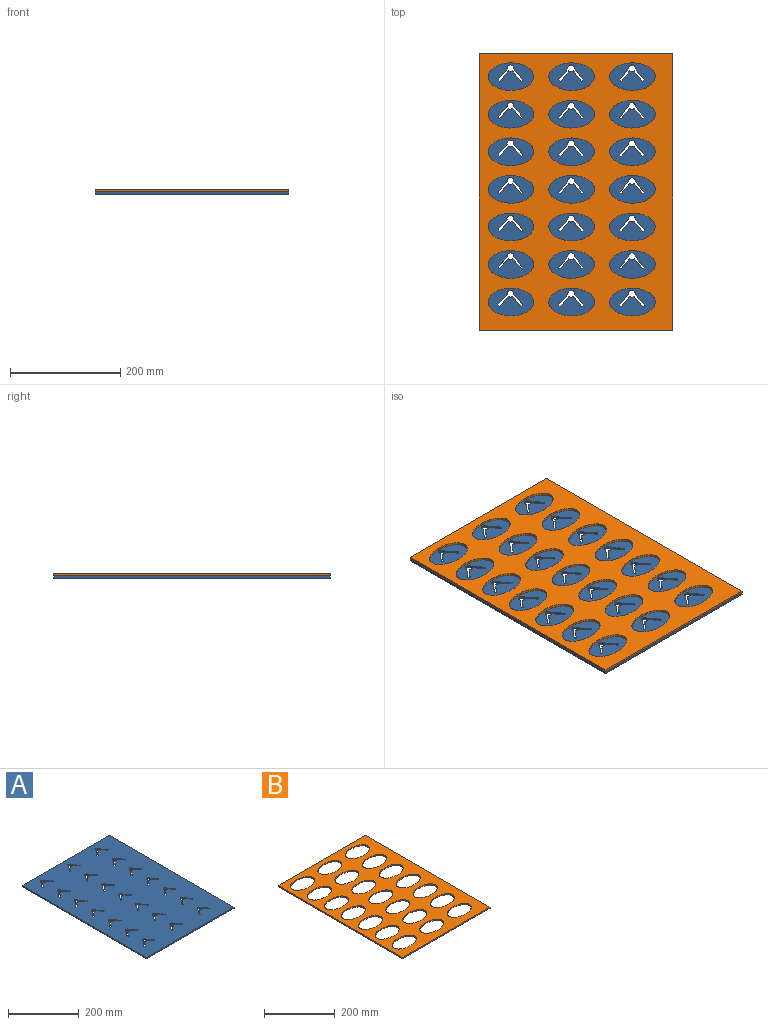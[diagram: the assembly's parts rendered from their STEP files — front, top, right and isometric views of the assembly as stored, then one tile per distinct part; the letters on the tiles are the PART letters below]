
ASSEMBLY  parts=2 mates=1
PART A: 174 faces, bbox 350x500x4 mm
  f0: plane 500x350mm, normal (0,0,1), area 168404.2mm2, adj f2,f3,f4,f5,f6,f7,f8,f9
  f1: plane 500x350mm, normal (0,0,-1), area 168404.2mm2, adj f2,f3,f4,f5,f6,f7,f8,f9
  f2: plane 350x4mm, normal (0,-1,0), area 1400mm2, adj f0,f1,f3,f5
  f3: plane 500x4mm, normal (1,0,0), area 2000mm2, adj f0,f1,f2,f4
  f4: plane 350x4mm, normal (0,1,0), area 1400mm2, adj f0,f1,f3,f5
  f5: plane 500x4mm, normal (-1,0,0), area 2000mm2, adj f0,f1,f2,f4
  f6: plane 19.38x16.26mm, normal (-0.77,-0.64,0), area 101.2mm2, adj f0,f1,f7,f13
  f7: cylinder r=6.17mm len=12.35mm, axis (0,0,1), area 85.9mm2, adj f0,f1,f6,f8
  f8: plane 19.38x16.26mm, normal (0.77,-0.64,0), area 101.2mm2, adj f0,f1,f7,f9
  f9: plane 4x3.06mm, normal (0.64,0.77,0), area 16mm2, adj f0,f1,f8,f10
  f10: plane 18.25x15.31mm, normal (-0.77,0.64,0), area 95.3mm2, adj f0,f1,f9,f11
  f11: cylinder r=6.17mm len=7.94mm, axis (0,0,1), area 34.5mm2, adj f0,f1,f10,f12
  f12: plane 18.25x15.31mm, normal (0.77,0.64,0), area 95.3mm2, adj f0,f1,f11,f13
  f13: plane 4x3.06mm, normal (-0.64,0.77,0), area 16mm2, adj f0,f1,f6,f12
  f14: cylinder r=6.17mm len=7.94mm, axis (0,0,1), area 34.5mm2, adj f0,f1,f15,f21
  f15: plane 18.25x15.31mm, normal (0.77,0.64,0), area 95.3mm2, adj f0,f1,f14,f16
  f16: plane 4x3.06mm, normal (-0.64,0.77,0), area 16mm2, adj f0,f1,f15,f17
  f17: plane 19.38x16.26mm, normal (-0.77,-0.64,0), area 101.2mm2, adj f0,f1,f16,f18
  f18: cylinder r=6.17mm len=12.35mm, axis (0,0,1), area 85.9mm2, adj f0,f1,f17,f19
  f19: plane 19.38x16.26mm, normal (0.77,-0.64,0), area 101.2mm2, adj f0,f1,f18,f20
  f20: plane 4x3.06mm, normal (0.64,0.77,0), area 16mm2, adj f0,f1,f19,f21
  f21: plane 18.25x15.31mm, normal (-0.77,0.64,0), area 95.3mm2, adj f0,f1,f14,f20
  f22: cylinder r=6.17mm len=7.94mm, axis (0,0,1), area 34.5mm2, adj f0,f1,f23,f29
  f23: plane 18.25x15.31mm, normal (0.77,0.64,0), area 95.3mm2, adj f0,f1,f22,f24
  f24: plane 4x3.06mm, normal (-0.64,0.77,0), area 16mm2, adj f0,f1,f23,f25
  f25: plane 19.38x16.26mm, normal (-0.77,-0.64,0), area 101.2mm2, adj f0,f1,f24,f26
  f26: cylinder r=6.17mm len=12.35mm, axis (0,0,1), area 85.9mm2, adj f0,f1,f25,f27
  f27: plane 19.38x16.26mm, normal (0.77,-0.64,0), area 101.2mm2, adj f0,f1,f26,f28
  f28: plane 4x3.06mm, normal (0.64,0.77,0), area 16mm2, adj f0,f1,f27,f29
  f29: plane 18.25x15.31mm, normal (-0.77,0.64,0), area 95.3mm2, adj f0,f1,f22,f28
  f30: cylinder r=6.17mm len=7.94mm, axis (0,0,1), area 34.5mm2, adj f0,f1,f31,f37
  f31: plane 18.25x15.31mm, normal (0.77,0.64,0), area 95.3mm2, adj f0,f1,f30,f32
  f32: plane 4x3.06mm, normal (-0.64,0.77,0), area 16mm2, adj f0,f1,f31,f33
  f33: plane 19.38x16.26mm, normal (-0.77,-0.64,0), area 101.2mm2, adj f0,f1,f32,f34
  f34: cylinder r=6.17mm len=12.35mm, axis (0,0,1), area 85.9mm2, adj f0,f1,f33,f35
  f35: plane 19.38x16.26mm, normal (0.77,-0.64,0), area 101.2mm2, adj f0,f1,f34,f36
  f36: plane 4x3.06mm, normal (0.64,0.77,0), area 16mm2, adj f0,f1,f35,f37
  f37: plane 18.25x15.31mm, normal (-0.77,0.64,0), area 95.3mm2, adj f0,f1,f30,f36
  f38: cylinder r=6.17mm len=7.94mm, axis (0,0,1), area 34.5mm2, adj f0,f1,f39,f45
  f39: plane 18.25x15.31mm, normal (0.77,0.64,0), area 95.3mm2, adj f0,f1,f38,f40
  f40: plane 4x3.06mm, normal (-0.64,0.77,0), area 16mm2, adj f0,f1,f39,f41
  f41: plane 19.38x16.26mm, normal (-0.77,-0.64,0), area 101.2mm2, adj f0,f1,f40,f42
  f42: cylinder r=6.17mm len=12.35mm, axis (0,0,1), area 85.9mm2, adj f0,f1,f41,f43
  f43: plane 19.38x16.26mm, normal (0.77,-0.64,0), area 101.2mm2, adj f0,f1,f42,f44
  f44: plane 4x3.06mm, normal (0.64,0.77,0), area 16mm2, adj f0,f1,f43,f45
  f45: plane 18.25x15.31mm, normal (-0.77,0.64,0), area 95.3mm2, adj f0,f1,f38,f44
  f46: cylinder r=6.17mm len=7.94mm, axis (0,0,1), area 34.5mm2, adj f0,f1,f47,f53
  f47: plane 18.25x15.31mm, normal (0.77,0.64,0), area 95.3mm2, adj f0,f1,f46,f48
  f48: plane 4x3.06mm, normal (-0.64,0.77,0), area 16mm2, adj f0,f1,f47,f49
  f49: plane 19.38x16.26mm, normal (-0.77,-0.64,0), area 101.2mm2, adj f0,f1,f48,f50
  f50: cylinder r=6.17mm len=12.35mm, axis (0,0,1), area 85.9mm2, adj f0,f1,f49,f51
  f51: plane 19.38x16.26mm, normal (0.77,-0.64,0), area 101.2mm2, adj f0,f1,f50,f52
  f52: plane 4x3.06mm, normal (0.64,0.77,0), area 16mm2, adj f0,f1,f51,f53
  f53: plane 18.25x15.31mm, normal (-0.77,0.64,0), area 95.3mm2, adj f0,f1,f46,f52
  f54: cylinder r=6.17mm len=7.94mm, axis (0,0,1), area 34.5mm2, adj f0,f1,f55,f61
  f55: plane 18.25x15.31mm, normal (0.77,0.64,0), area 95.3mm2, adj f0,f1,f54,f56
  f56: plane 4x3.06mm, normal (-0.64,0.77,0), area 16mm2, adj f0,f1,f55,f57
  f57: plane 19.38x16.26mm, normal (-0.77,-0.64,0), area 101.2mm2, adj f0,f1,f56,f58
  f58: cylinder r=6.17mm len=12.35mm, axis (0,0,1), area 85.9mm2, adj f0,f1,f57,f59
  f59: plane 19.38x16.26mm, normal (0.77,-0.64,0), area 101.2mm2, adj f0,f1,f58,f60
  f60: plane 4x3.06mm, normal (0.64,0.77,0), area 16mm2, adj f0,f1,f59,f61
  f61: plane 18.25x15.31mm, normal (-0.77,0.64,0), area 95.3mm2, adj f0,f1,f54,f60
  f62: cylinder r=6.17mm len=7.94mm, axis (0,0,1), area 34.5mm2, adj f0,f1,f63,f69
  f63: plane 18.25x15.31mm, normal (0.77,0.64,0), area 95.3mm2, adj f0,f1,f62,f64
  f64: plane 4x3.06mm, normal (-0.64,0.77,0), area 16mm2, adj f0,f1,f63,f65
  f65: plane 19.38x16.26mm, normal (-0.77,-0.64,0), area 101.2mm2, adj f0,f1,f64,f66
  f66: cylinder r=6.17mm len=12.35mm, axis (0,0,1), area 85.9mm2, adj f0,f1,f65,f67
  f67: plane 19.38x16.26mm, normal (0.77,-0.64,0), area 101.2mm2, adj f0,f1,f66,f68
  f68: plane 4x3.06mm, normal (0.64,0.77,0), area 16mm2, adj f0,f1,f67,f69
  f69: plane 18.25x15.31mm, normal (-0.77,0.64,0), area 95.3mm2, adj f0,f1,f62,f68
  f70: cylinder r=6.17mm len=7.94mm, axis (0,0,1), area 34.5mm2, adj f0,f1,f71,f77
  f71: plane 18.25x15.31mm, normal (0.77,0.64,0), area 95.3mm2, adj f0,f1,f70,f72
  f72: plane 4x3.06mm, normal (-0.64,0.77,0), area 16mm2, adj f0,f1,f71,f73
  f73: plane 19.38x16.26mm, normal (-0.77,-0.64,0), area 101.2mm2, adj f0,f1,f72,f74
  f74: cylinder r=6.17mm len=12.35mm, axis (0,0,1), area 85.9mm2, adj f0,f1,f73,f75
  f75: plane 19.38x16.26mm, normal (0.77,-0.64,0), area 101.2mm2, adj f0,f1,f74,f76
  f76: plane 4x3.06mm, normal (0.64,0.77,0), area 16mm2, adj f0,f1,f75,f77
  f77: plane 18.25x15.31mm, normal (-0.77,0.64,0), area 95.3mm2, adj f0,f1,f70,f76
  f78: cylinder r=6.17mm len=7.94mm, axis (0,0,1), area 34.5mm2, adj f0,f1,f79,f85
  f79: plane 18.25x15.31mm, normal (0.77,0.64,0), area 95.3mm2, adj f0,f1,f78,f80
  f80: plane 4x3.06mm, normal (-0.64,0.77,0), area 16mm2, adj f0,f1,f79,f81
  f81: plane 19.38x16.26mm, normal (-0.77,-0.64,0), area 101.2mm2, adj f0,f1,f80,f82
  f82: cylinder r=6.17mm len=12.35mm, axis (0,0,1), area 85.9mm2, adj f0,f1,f81,f83
  f83: plane 19.38x16.26mm, normal (0.77,-0.64,0), area 101.2mm2, adj f0,f1,f82,f84
  f84: plane 4x3.06mm, normal (0.64,0.77,0), area 16mm2, adj f0,f1,f83,f85
  f85: plane 18.25x15.31mm, normal (-0.77,0.64,0), area 95.3mm2, adj f0,f1,f78,f84
  f86: cylinder r=6.17mm len=7.94mm, axis (0,0,1), area 34.5mm2, adj f0,f1,f87,f93
  f87: plane 18.25x15.31mm, normal (0.77,0.64,0), area 95.3mm2, adj f0,f1,f86,f88
  f88: plane 4x3.06mm, normal (-0.64,0.77,0), area 16mm2, adj f0,f1,f87,f89
  f89: plane 19.38x16.26mm, normal (-0.77,-0.64,0), area 101.2mm2, adj f0,f1,f88,f90
  f90: cylinder r=6.17mm len=12.35mm, axis (0,0,1), area 85.9mm2, adj f0,f1,f89,f91
  f91: plane 19.38x16.26mm, normal (0.77,-0.64,0), area 101.2mm2, adj f0,f1,f90,f92
  f92: plane 4x3.06mm, normal (0.64,0.77,0), area 16mm2, adj f0,f1,f91,f93
  f93: plane 18.25x15.31mm, normal (-0.77,0.64,0), area 95.3mm2, adj f0,f1,f86,f92
  f94: cylinder r=6.17mm len=7.94mm, axis (0,0,1), area 34.5mm2, adj f0,f1,f95,f101
  f95: plane 18.25x15.31mm, normal (0.77,0.64,0), area 95.3mm2, adj f0,f1,f94,f96
  f96: plane 4x3.06mm, normal (-0.64,0.77,0), area 16mm2, adj f0,f1,f95,f97
  f97: plane 19.38x16.26mm, normal (-0.77,-0.64,0), area 101.2mm2, adj f0,f1,f96,f98
  f98: cylinder r=6.17mm len=12.35mm, axis (0,0,1), area 85.9mm2, adj f0,f1,f97,f99
  f99: plane 19.38x16.26mm, normal (0.77,-0.64,0), area 101.2mm2, adj f0,f1,f98,f100
  f100: plane 4x3.06mm, normal (0.64,0.77,0), area 16mm2, adj f0,f1,f99,f101
  f101: plane 18.25x15.31mm, normal (-0.77,0.64,0), area 95.3mm2, adj f0,f1,f94,f100
  f102: plane 4x3.06mm, normal (0.64,0.77,0), area 16mm2, adj f0,f1,f103,f109
  f103: plane 18.25x15.31mm, normal (-0.77,0.64,0), area 95.3mm2, adj f0,f1,f102,f104
  f104: cylinder r=6.17mm len=7.94mm, axis (0,0,1), area 34.5mm2, adj f0,f1,f103,f105
  f105: plane 18.25x15.31mm, normal (0.77,0.64,0), area 95.3mm2, adj f0,f1,f104,f106
  f106: plane 4x3.06mm, normal (-0.64,0.77,0), area 16mm2, adj f0,f1,f105,f107
  f107: plane 19.38x16.26mm, normal (-0.77,-0.64,0), area 101.2mm2, adj f0,f1,f106,f108
  f108: cylinder r=6.17mm len=12.35mm, axis (0,0,1), area 85.9mm2, adj f0,f1,f107,f109
  f109: plane 19.38x16.26mm, normal (0.77,-0.64,0), area 101.2mm2, adj f0,f1,f102,f108
  f110: cylinder r=6.17mm len=7.94mm, axis (0,0,1), area 34.5mm2, adj f0,f1,f111,f117
  f111: plane 18.25x15.31mm, normal (0.77,0.64,0), area 95.3mm2, adj f0,f1,f110,f112
  f112: plane 4x3.06mm, normal (-0.64,0.77,0), area 16mm2, adj f0,f1,f111,f113
  f113: plane 19.38x16.26mm, normal (-0.77,-0.64,0), area 101.2mm2, adj f0,f1,f112,f114
  f114: cylinder r=6.17mm len=12.35mm, axis (0,0,1), area 85.9mm2, adj f0,f1,f113,f115
  f115: plane 19.38x16.26mm, normal (0.77,-0.64,0), area 101.2mm2, adj f0,f1,f114,f116
  f116: plane 4x3.06mm, normal (0.64,0.77,0), area 16mm2, adj f0,f1,f115,f117
  f117: plane 18.25x15.31mm, normal (-0.77,0.64,0), area 95.3mm2, adj f0,f1,f110,f116
  f118: cylinder r=6.17mm len=7.94mm, axis (0,0,1), area 34.5mm2, adj f0,f1,f119,f125
  f119: plane 18.25x15.31mm, normal (0.77,0.64,0), area 95.3mm2, adj f0,f1,f118,f120
  f120: plane 4x3.06mm, normal (-0.64,0.77,0), area 16mm2, adj f0,f1,f119,f121
  f121: plane 19.38x16.26mm, normal (-0.77,-0.64,0), area 101.2mm2, adj f0,f1,f120,f122
  f122: cylinder r=6.17mm len=12.35mm, axis (0,0,1), area 85.9mm2, adj f0,f1,f121,f123
  f123: plane 19.38x16.26mm, normal (0.77,-0.64,0), area 101.2mm2, adj f0,f1,f122,f124
  f124: plane 4x3.06mm, normal (0.64,0.77,0), area 16mm2, adj f0,f1,f123,f125
  f125: plane 18.25x15.31mm, normal (-0.77,0.64,0), area 95.3mm2, adj f0,f1,f118,f124
  f126: cylinder r=6.17mm len=7.94mm, axis (0,0,1), area 34.5mm2, adj f0,f1,f127,f133
  f127: plane 18.25x15.31mm, normal (0.77,0.64,0), area 95.3mm2, adj f0,f1,f126,f128
  f128: plane 4x3.06mm, normal (-0.64,0.77,0), area 16mm2, adj f0,f1,f127,f129
  f129: plane 19.38x16.26mm, normal (-0.77,-0.64,0), area 101.2mm2, adj f0,f1,f128,f130
  f130: cylinder r=6.17mm len=12.35mm, axis (0,0,1), area 85.9mm2, adj f0,f1,f129,f131
  f131: plane 19.38x16.26mm, normal (0.77,-0.64,0), area 101.2mm2, adj f0,f1,f130,f132
  f132: plane 4x3.06mm, normal (0.64,0.77,0), area 16mm2, adj f0,f1,f131,f133
  f133: plane 18.25x15.31mm, normal (-0.77,0.64,0), area 95.3mm2, adj f0,f1,f126,f132
  f134: cylinder r=6.17mm len=7.94mm, axis (0,0,1), area 34.5mm2, adj f0,f1,f135,f141
  f135: plane 18.25x15.31mm, normal (0.77,0.64,0), area 95.3mm2, adj f0,f1,f134,f136
  f136: plane 4x3.06mm, normal (-0.64,0.77,0), area 16mm2, adj f0,f1,f135,f137
  f137: plane 19.38x16.26mm, normal (-0.77,-0.64,0), area 101.2mm2, adj f0,f1,f136,f138
  f138: cylinder r=6.17mm len=12.35mm, axis (0,0,1), area 85.9mm2, adj f0,f1,f137,f139
  f139: plane 19.38x16.26mm, normal (0.77,-0.64,0), area 101.2mm2, adj f0,f1,f138,f140
  f140: plane 4x3.06mm, normal (0.64,0.77,0), area 16mm2, adj f0,f1,f139,f141
  f141: plane 18.25x15.31mm, normal (-0.77,0.64,0), area 95.3mm2, adj f0,f1,f134,f140
  f142: cylinder r=6.17mm len=7.94mm, axis (0,0,1), area 34.5mm2, adj f0,f1,f143,f149
  f143: plane 18.25x15.31mm, normal (0.77,0.64,0), area 95.3mm2, adj f0,f1,f142,f144
  f144: plane 4x3.06mm, normal (-0.64,0.77,0), area 16mm2, adj f0,f1,f143,f145
  f145: plane 19.38x16.26mm, normal (-0.77,-0.64,0), area 101.2mm2, adj f0,f1,f144,f146
  f146: cylinder r=6.17mm len=12.35mm, axis (0,0,1), area 85.9mm2, adj f0,f1,f145,f147
  f147: plane 19.38x16.26mm, normal (0.77,-0.64,0), area 101.2mm2, adj f0,f1,f146,f148
  f148: plane 4x3.06mm, normal (0.64,0.77,0), area 16mm2, adj f0,f1,f147,f149
  f149: plane 18.25x15.31mm, normal (-0.77,0.64,0), area 95.3mm2, adj f0,f1,f142,f148
  f150: cylinder r=6.17mm len=7.94mm, axis (0,0,1), area 34.5mm2, adj f0,f1,f151,f157
  f151: plane 18.25x15.31mm, normal (0.77,0.64,0), area 95.3mm2, adj f0,f1,f150,f152
  f152: plane 4x3.06mm, normal (-0.64,0.77,0), area 16mm2, adj f0,f1,f151,f153
  f153: plane 19.38x16.26mm, normal (-0.77,-0.64,0), area 101.2mm2, adj f0,f1,f152,f154
  f154: cylinder r=6.17mm len=12.35mm, axis (0,0,1), area 85.9mm2, adj f0,f1,f153,f155
  f155: plane 19.38x16.26mm, normal (0.77,-0.64,0), area 101.2mm2, adj f0,f1,f154,f156
  f156: plane 4x3.06mm, normal (0.64,0.77,0), area 16mm2, adj f0,f1,f155,f157
  f157: plane 18.25x15.31mm, normal (-0.77,0.64,0), area 95.3mm2, adj f0,f1,f150,f156
  f158: cylinder r=6.17mm len=7.94mm, axis (0,0,1), area 34.5mm2, adj f0,f1,f159,f165
  f159: plane 18.25x15.31mm, normal (0.77,0.64,0), area 95.3mm2, adj f0,f1,f158,f160
  f160: plane 4x3.06mm, normal (-0.64,0.77,0), area 16mm2, adj f0,f1,f159,f161
  f161: plane 19.38x16.26mm, normal (-0.77,-0.64,0), area 101.2mm2, adj f0,f1,f160,f162
  f162: cylinder r=6.17mm len=12.35mm, axis (0,0,1), area 85.9mm2, adj f0,f1,f161,f163
  f163: plane 19.38x16.26mm, normal (0.77,-0.64,0), area 101.2mm2, adj f0,f1,f162,f164
  f164: plane 4x3.06mm, normal (0.64,0.77,0), area 16mm2, adj f0,f1,f163,f165
  f165: plane 18.25x15.31mm, normal (-0.77,0.64,0), area 95.3mm2, adj f0,f1,f158,f164
  f166: cylinder r=6.17mm len=7.94mm, axis (0,0,1), area 34.5mm2, adj f0,f1,f167,f173
  f167: plane 18.25x15.31mm, normal (0.77,0.64,0), area 95.3mm2, adj f0,f1,f166,f168
  f168: plane 4x3.06mm, normal (-0.64,0.77,0), area 16mm2, adj f0,f1,f167,f169
  f169: plane 19.38x16.26mm, normal (-0.77,-0.64,0), area 101.2mm2, adj f0,f1,f168,f170
  f170: cylinder r=6.17mm len=12.35mm, axis (0,0,1), area 85.9mm2, adj f0,f1,f169,f171
  f171: plane 19.38x16.26mm, normal (0.77,-0.64,0), area 101.2mm2, adj f0,f1,f170,f172
  f172: plane 4x3.06mm, normal (0.64,0.77,0), area 16mm2, adj f0,f1,f171,f173
  f173: plane 18.25x15.31mm, normal (-0.77,0.64,0), area 95.3mm2, adj f0,f1,f166,f172
PART B: 27 faces, bbox 350x500x4 mm
  f0: plane 350x4mm, normal (0,-1,0), area 1400mm2, adj f1,f3,f4,f5
  f1: plane 500x4mm, normal (1,0,0), area 2000mm2, adj f0,f2,f4,f5
  f2: plane 350x4mm, normal (0,1,0), area 1400mm2, adj f1,f3,f4,f5
  f3: plane 500x4mm, normal (-1,0,0), area 2000mm2, adj f0,f2,f4,f5
  f4: plane 500x350mm, normal (0,0,1), area 107068.3mm2, adj f0,f1,f2,f3,f6,f7,f8,f9
  f5: plane 500x350mm, normal (0,0,-1), area 107068.3mm2, adj f0,f1,f2,f3,f6,f7,f8,f9
  f6: extruded ~82.37x50mm, area 844.2mm2, adj f4,f5
  f7: extruded ~82.37x50mm, area 844.2mm2, adj f4,f5
  f8: extruded ~82.37x50mm, area 844.2mm2, adj f4,f5
  f9: extruded ~82.37x50mm, area 844.2mm2, adj f4,f5
  f10: extruded ~82.37x50mm, area 844.2mm2, adj f4,f5
  f11: extruded ~82.37x50mm, area 844.2mm2, adj f4,f5
  f12: extruded ~82.37x50mm, area 844.2mm2, adj f4,f5
  f13: extruded ~82.37x50mm, area 844.2mm2, adj f4,f5
  f14: extruded ~82.37x50mm, area 844.2mm2, adj f4,f5
  f15: extruded ~82.37x50mm, area 844.2mm2, adj f4,f5
  f16: extruded ~82.37x50mm, area 844.2mm2, adj f4,f5
  f17: extruded ~82.37x50mm, area 844.2mm2, adj f4,f5
  f18: extruded ~82.37x50mm, area 844.2mm2, adj f4,f5
  f19: extruded ~82.37x50mm, area 844.2mm2, adj f4,f5
  f20: extruded ~82.37x50mm, area 844.2mm2, adj f4,f5
  f21: extruded ~82.37x50mm, area 844.2mm2, adj f4,f5
  f22: extruded ~82.37x50mm, area 844.2mm2, adj f4,f5
  f23: extruded ~82.37x50mm, area 844.2mm2, adj f4,f5
  f24: extruded ~82.37x50mm, area 844.2mm2, adj f4,f5
  f25: extruded ~82.37x50mm, area 844.2mm2, adj f4,f5
  f26: extruded ~82.37x50mm, area 844.2mm2, adj f4,f5
PLACE A t=(-58.3,-16.87,23.18)mm
PLACE B t=(-58.3,-16.87,27.18)mm
MATE parallel B.f5 <-> A.f0  axis (0,0,-1) through (-58.3,233.13,27.18)mm
